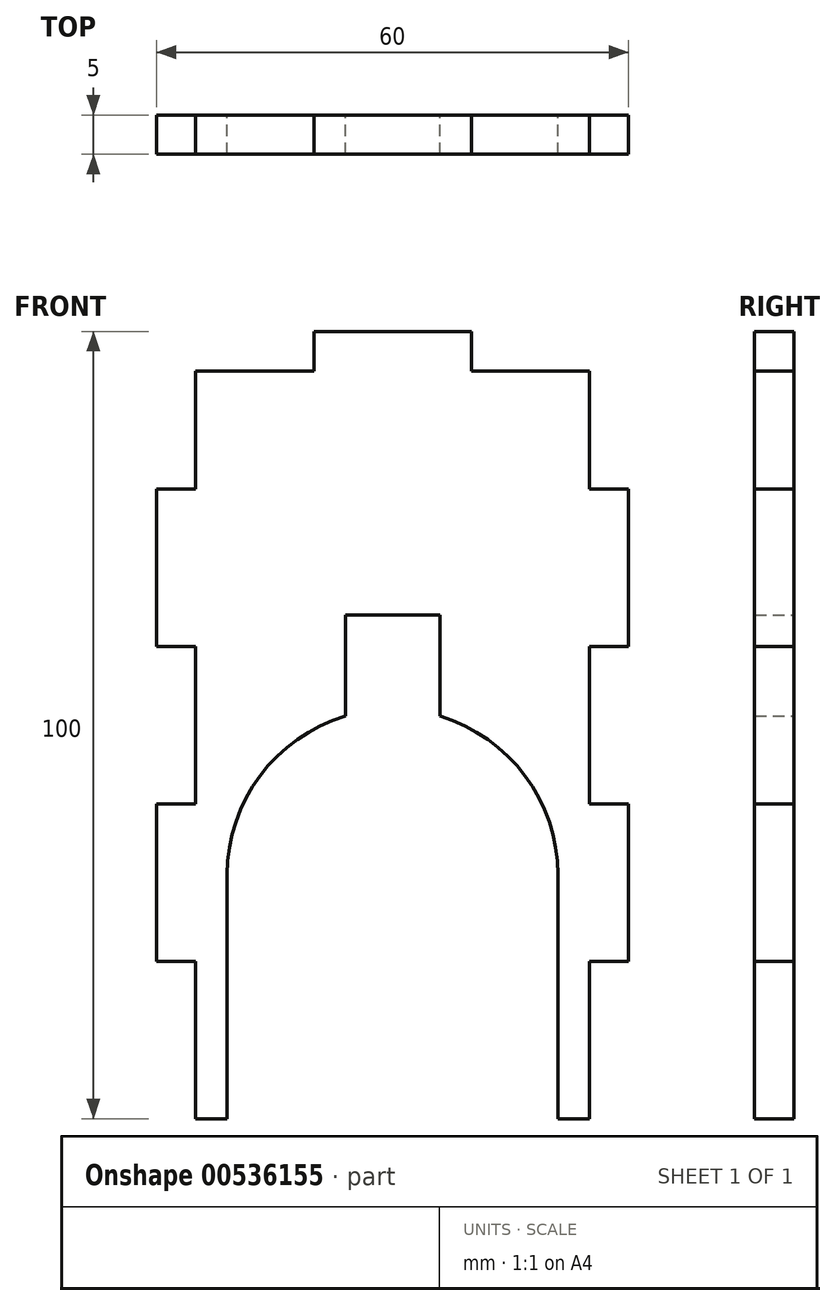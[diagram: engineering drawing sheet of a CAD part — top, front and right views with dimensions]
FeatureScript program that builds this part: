
annotation { "Feature Type Name" : "Feature", "Feature Type Description" : "" }
export const myFeature = defineFeature(function(context is Context, id is Id, definition is map)
    precondition{}
    {
        {
            var Q0;
            Q0=qCreatedBy(makeId("Front.planeOp"),FACE);
            var sketch = newSketch(context, id + "F0", { "sketchPlane" : qUnion([Q0])});
            skLineSegment(sketch, "E0.bottom", {"start": v(25, 53.43) * mm, "end": v(10, 53.43) * mm});
            skLineSegment(sketch, "E0.left", {"start": v(25, 53.43) * mm, "end": v(25, 38.43) * mm});
            skLineSegment(sketch, "E0.right", {"start": v(-25, 53.43) * mm, "end": v(-25, 38.43) * mm});
            skPoint(sketch, "E0.middle", {"position": v(0, 5.93) * mm});
            skLineSegment(sketch, "E1", {"start": v(-30, -41.57) * mm, "end": v(-30, 58.43) * mm, "construction": true});
            skLineSegment(sketch, "E2", {"start": v(-30, 58.43) * mm, "end": v(30, 58.43) * mm, "construction": true});
            skLineSegment(sketch, "E3", {"start": v(30, 58.43) * mm, "end": v(30, -41.57) * mm, "construction": true});
            skLineSegment(sketch, "E4", {"start": v(25, -21.57) * mm, "end": v(30, -21.57) * mm});
            skLineSegment(sketch, "E5", {"start": v(30, -21.57) * mm, "end": v(30, -1.57) * mm});
            skLineSegment(sketch, "E6", {"start": v(30, -1.57) * mm, "end": v(25, -1.57) * mm});
            skLineSegment(sketch, "E7", {"start": v(25, 18.43) * mm, "end": v(30, 18.43) * mm});
            skLineSegment(sketch, "E8", {"start": v(30, 18.43) * mm, "end": v(30, 38.43) * mm});
            skLineSegment(sketch, "E9", {"start": v(30, 38.43) * mm, "end": v(25, 38.43) * mm});
            skLineSegment(sketch, "E10.trimOffspring", {"start": v(25, 18.43) * mm, "end": v(25, -1.57) * mm});
            skLineSegment(sketch, "E11.trimOffspring", {"start": v(25, -21.57) * mm, "end": v(25, -29.57) * mm});
            skLineSegment(sketch, "E12.MirrorCS", {"start": v(-30, 38.43) * mm, "end": v(-25, 38.43) * mm});
            skLineSegment(sketch, "E13.MirrorCS", {"start": v(-25, 18.43) * mm, "end": v(-30, 18.43) * mm});
            skLineSegment(sketch, "E14.MirrorCS", {"start": v(-30, -1.57) * mm, "end": v(-25, -1.57) * mm});
            skLineSegment(sketch, "E15.MirrorCS", {"start": v(-25, -21.57) * mm, "end": v(-30, -21.57) * mm});
            skLineSegment(sketch, "E16", {"start": v(-30, 38.43) * mm, "end": v(-30, 18.43) * mm});
            skLineSegment(sketch, "E17", {"start": v(-30, -1.57) * mm, "end": v(-30, -21.57) * mm});
            skLineSegment(sketch, "E18.trimOffspring", {"start": v(-25, 18.43) * mm, "end": v(-25, -1.57) * mm});
            skLineSegment(sketch, "E19.trimOffspring", {"start": v(-25, -21.57) * mm, "end": v(-25, -29.57) * mm});
            skLineSegment(sketch, "E20", {"start": v(-10, 53.43) * mm, "end": v(-10, 58.43) * mm});
            skLineSegment(sketch, "E21", {"start": v(-10, 58.43) * mm, "end": v(10, 58.43) * mm});
            skLineSegment(sketch, "E22", {"start": v(10, 58.43) * mm, "end": v(10, 53.43) * mm});
            skLineSegment(sketch, "E23.trimOffspring", {"start": v(-10, 53.43) * mm, "end": v(-25, 53.43) * mm});
            skPoint(sketch, "E24.middle", {"position": v(0, -41.57) * mm});
            skLineSegment(sketch, "E25", {"start": v(-21, -20.57) * mm, "end": v(-21, -29.57) * mm});
            skLineSegment(sketch, "E26", {"start": v(21, -20.57) * mm, "end": v(21, -29.57) * mm});
            skPoint(sketch, "E27.trimOffspring.end.orphan", {"position": v(-25, -41.57) * mm});
            skPoint(sketch, "E0.top.start.orphan", {"position": v(25, -41.57) * mm});
            skPoint(sketch, "E28.orphan", {"position": v(-21, -31.57) * mm});
            skPoint(sketch, "E29.start.orphan", {"position": v(21, -31.57) * mm});
            skPoint(sketch, "E30.orphan", {"position": v(25, -31.57) * mm});
            skLineSegment(sketch, "E31", {"start": v(-25, -29.57) * mm, "end": v(-25, -41.57) * mm});
            skLineSegment(sketch, "E32", {"start": v(-25, -41.57) * mm, "end": v(-21, -41.57) * mm});
            skLineSegment(sketch, "E33", {"start": v(-21, -41.57) * mm, "end": v(-21, -29.57) * mm});
            skLineSegment(sketch, "E34", {"start": v(21, -29.57) * mm, "end": v(21, -41.57) * mm});
            skLineSegment(sketch, "E35", {"start": v(21, -41.57) * mm, "end": v(25, -41.57) * mm});
            skLineSegment(sketch, "E36", {"start": v(25, -41.57) * mm, "end": v(25, -29.57) * mm});
            skArc(sketch, "E37", {"start": v(21, -10.57) * mm, "mid": v(16.84, 1.98) * mm, "end": v(6, 9.56) * mm});
            skLineSegment(sketch, "E38", {"start": v(-21, -10.57) * mm, "end": v(-21, -20.57) * mm});
            skLineSegment(sketch, "E39", {"start": v(21, -10.57) * mm, "end": v(21, -20.57) * mm});
            skPoint(sketch, "E40.center.orphan", {"position": v(0, -20.57) * mm});
            skLineSegment(sketch, "E41.top", {"start": v(-6, 22.43) * mm, "end": v(6, 22.43) * mm});
            skLineSegment(sketch, "E41.left", {"start": v(-6, 10.43) * mm, "end": v(-6, 22.43) * mm});
            skLineSegment(sketch, "E41.right", {"start": v(6, 10.43) * mm, "end": v(6, 22.43) * mm});
            skPoint(sketch, "E41.middle", {"position": v(0, 16.43) * mm});
            skPoint(sketch, "E41.cornerSnap0", {"position": v(0, 10.43) * mm});
            skLineSegment(sketch, "E42", {"start": v(-6, 10.43) * mm, "end": v(-6, 9.56) * mm});
            skLineSegment(sketch, "E43", {"start": v(6, 10.43) * mm, "end": v(6, 9.56) * mm});
            skArc(sketch, "E44.trimOffspring", {"start": v(-6, 9.56) * mm, "mid": v(-16.84, 1.98) * mm, "end": v(-21, -10.57) * mm});
            skSolve(sketch);
        }
        {
            var Q0;
            Q0 = qSketchRegion(id + "F0", true);
            extrude(context, id + "F1", {"entities" : qUnion([Q0]), "depth" : 5 * mm, "offsetDistance" : 25 * mm});
        }
    });
